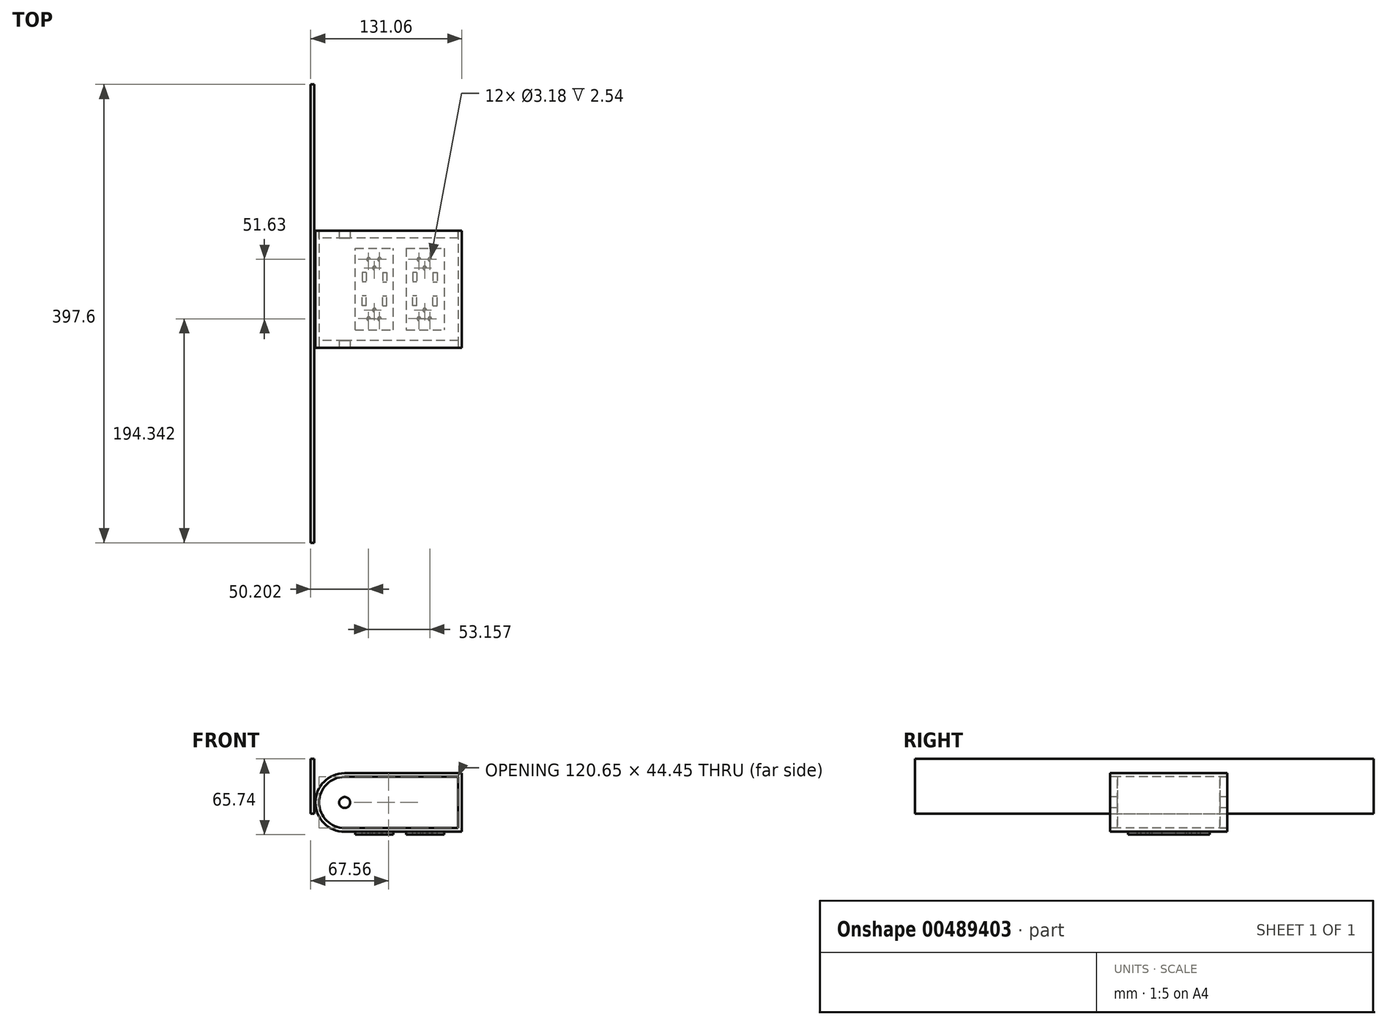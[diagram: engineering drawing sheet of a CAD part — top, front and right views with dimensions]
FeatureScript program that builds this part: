
annotation { "Feature Type Name" : "Feature", "Feature Type Description" : "" }
export const myFeature = defineFeature(function(context is Context, id is Id, definition is map)
    precondition{}
    {
        {
            var Q0;
            Q0=qCreatedBy(makeId("Front.planeOp"),FACE);
            var sketch = newSketch(context, id + "F0", { "sketchPlane" : qUnion([Q0])});
            skLineSegment(sketch, "E0.bottom", {"start": v(0, 0) * mm, "end": v(-101.6, 0) * mm});
            skLineSegment(sketch, "E0.top", {"start": v(0, 50.8) * mm, "end": v(-101.6, 50.8) * mm});
            skLineSegment(sketch, "E0.left", {"start": v(0, 0) * mm, "end": v(0, 50.8) * mm});
            skArc(sketch, "E1", {"start": v(-101.6, 50.8) * mm, "mid": v(-127, 25.4) * mm, "end": v(-101.6, 0) * mm});
            skPoint(sketch, "E1.centerSnap0", {"position": v(-127, 25.4) * mm});
            skArc(sketch, "E2.0", {"start": v(-101.6, 47.62) * mm, "mid": v(-123.83, 25.4) * mm, "end": v(-101.6, 3.18) * mm});
            skLineSegment(sketch, "E2.1", {"start": v(-3.18, 47.62) * mm, "end": v(-101.6, 47.62) * mm});
            skLineSegment(sketch, "E2.2", {"start": v(-3.17, 3.18) * mm, "end": v(-3.18, 47.62) * mm});
            skLineSegment(sketch, "E2.3", {"start": v(-3.17, 3.18) * mm, "end": v(-101.6, 3.17) * mm});
            skCircle(sketch, "E3", {"center": v(-101.6, 25.4) * mm, "radius": 4.76 * mm});
            skSolve(sketch);
        }
        {
            var Q0;
            Q0=makeQuery(id+"F0.imprint","IMPRINT",FACE,{"disambiguationData":[TD([[makeQuery(id+"F0.imprint","IMPRINT",EDGE,{"derivedFrom":sQuery(id+"F0.wireOp",EDGE,"E0.bottom")}),-1.0]])]});
            extrude(context, id + "F1", {"entities" : qUnion([Q0]), "oppositeDirection" : true, "depth" : 101.6 * mm, "offsetDistance" : 25.4 * mm});
        }
        {
            var Q0;
            Q0=makeQuery(id+"F0.imprint","IMPRINT",FACE,{"disambiguationData":[TD([[makeQuery(id+"F0.imprint","IMPRINT",EDGE,{"derivedFrom":sQuery(id+"F0.wireOp",EDGE,"E2.0")}),1.0]])]});
            extrude(context, id + "F2", {"entities" : qUnion([Q0]), "oppositeDirection" : true, "depth" : 6.35 * mm, "offsetDistance" : 25.4 * mm});
        }
        {
            var Q0;
            Q0=makeQuery(id+"F1.opExtrude","CAP_FACE",FACE,{"disambiguationData":[OSD([sQuery(id+"F0.wireOp",EDGE,"E0.bottom"),sQuery(id+"F0.wireOp",EDGE,"E0.top"),sQuery(id+"F0.wireOp",EDGE,"E0.left"),sQuery(id+"F0.wireOp",EDGE,"E1"),sQuery(id+"F0.wireOp",EDGE,"E2.0"),sQuery(id+"F0.wireOp",EDGE,"E2.1"),sQuery(id+"F0.wireOp",EDGE,"E2.2"),sQuery(id+"F0.wireOp",EDGE,"E2.3")])],"isStart":false});
            var sketch = newSketch(context, id + "F3", { "sketchPlane" : qUnion([Q0])});
            skSolve(sketch);
        }
        {
            var Q0;
            Q0=makeQuery(id+"F3.imprint","IMPRINT",FACE,{"disambiguationData":[TD([[makeQuery(id+"F3.imprint","IMPRINT",EDGE,{"derivedFrom":makeQuery(id+"F1.opExtrude","CAP_EDGE",EDGE,{"disambiguationData":[OSD([sQuery(id+"F0.wireOp",EDGE,"E2.0")])],"isStart":false})}),-1.0]])]});
            extrude(context, id + "F4", {"entities" : qUnion([Q0]), "oppositeDirection" : true, "depth" : 6.35 * mm, "offsetDistance" : 25.4 * mm});
        }
        {
            var Q0;
            Q0=makeQuery(id+"F1.opExtrude","SWEPT_FACE",FACE,{"disambiguationData":[OSD([sQuery(id+"F0.wireOp",EDGE,"E0.bottom")])]});
            var sketch = newSketch(context, id + "F5", { "sketchPlane" : qUnion([Q0])});
            skLineSegment(sketch, "E4.bottom", {"start": v(-92.53, -15.52) * mm, "end": v(-59.53, -15.52) * mm});
            skLineSegment(sketch, "E4.top", {"start": v(-92.53, -86.52) * mm, "end": v(-59.53, -86.52) * mm});
            skLineSegment(sketch, "E4.left", {"start": v(-92.53, -15.52) * mm, "end": v(-92.53, -86.52) * mm});
            skLineSegment(sketch, "E4.right", {"start": v(-59.53, -15.52) * mm, "end": v(-59.53, -86.52) * mm});
            skLineSegment(sketch, "E5.bottom", {"start": v(-48.24, -86.52) * mm, "end": v(-15.25, -86.52) * mm});
            skLineSegment(sketch, "E5.top", {"start": v(-48.24, -15.52) * mm, "end": v(-15.25, -15.52) * mm});
            skLineSegment(sketch, "E5.left", {"start": v(-48.24, -86.52) * mm, "end": v(-48.24, -15.52) * mm});
            skLineSegment(sketch, "E5.right", {"start": v(-15.25, -86.52) * mm, "end": v(-15.25, -15.52) * mm});
            skCircle(sketch, "E6", {"center": v(-80.86, -25.3) * mm, "radius": 1.59 * mm});
            skCircle(sketch, "E7", {"center": v(-71.39, -25.2) * mm, "radius": 1.59 * mm});
            skCircle(sketch, "E8", {"center": v(-75.83, -32.77) * mm, "radius": 1.59 * mm});
            skLineSegment(sketch, "E9.bottom", {"start": v(-68.76, -36.47) * mm, "end": v(-65.13, -36.47) * mm});
            skLineSegment(sketch, "E9.top", {"start": v(-68.76, -44.95) * mm, "end": v(-65.13, -44.95) * mm});
            skLineSegment(sketch, "E9.left", {"start": v(-68.76, -36.47) * mm, "end": v(-68.76, -44.95) * mm});
            skLineSegment(sketch, "E9.right", {"start": v(-65.13, -36.47) * mm, "end": v(-65.13, -44.95) * mm});
            skLineSegment(sketch, "E10.bottom", {"start": v(-82.86, -36.47) * mm, "end": v(-86.27, -36.47) * mm});
            skLineSegment(sketch, "E10.top", {"start": v(-82.86, -44.95) * mm, "end": v(-86.27, -44.95) * mm});
            skLineSegment(sketch, "E10.left", {"start": v(-82.86, -36.47) * mm, "end": v(-82.86, -44.95) * mm});
            skLineSegment(sketch, "E10.right", {"start": v(-86.27, -36.47) * mm, "end": v(-86.27, -44.95) * mm});
            skLineSegment(sketch, "E11.1.0.0", {"start": v(-25.08, -36.47) * mm, "end": v(-25.08, -44.95) * mm});
            skLineSegment(sketch, "E11.1.0.1", {"start": v(-21.44, -36.47) * mm, "end": v(-21.44, -44.95) * mm});
            skCircle(sketch, "E11.1.0.2", {"center": v(-32.14, -32.77) * mm, "radius": 1.59 * mm});
            skLineSegment(sketch, "E11.1.0.3", {"start": v(-42.58, -36.47) * mm, "end": v(-42.58, -44.95) * mm});
            skCircle(sketch, "E11.1.0.4", {"center": v(-37.17, -25.3) * mm, "radius": 1.59 * mm});
            skCircle(sketch, "E11.1.0.5", {"center": v(-27.7, -25.2) * mm, "radius": 1.59 * mm});
            skLineSegment(sketch, "E11.1.0.6", {"start": v(-39.17, -36.47) * mm, "end": v(-39.17, -44.95) * mm});
            skLineSegment(sketch, "E11.1.0.7", {"start": v(-39.17, -36.47) * mm, "end": v(-42.58, -36.47) * mm});
            skLineSegment(sketch, "E11.1.0.8", {"start": v(-25.08, -36.47) * mm, "end": v(-21.44, -36.47) * mm});
            skLineSegment(sketch, "E11.1.0.9", {"start": v(-25.08, -44.95) * mm, "end": v(-21.44, -44.95) * mm});
            skLineSegment(sketch, "E11.1.0.10", {"start": v(-39.17, -44.95) * mm, "end": v(-42.58, -44.95) * mm});
            skLineSegment(sketch, "E11.direction1", {"start": v(-86.27, -44.95) * mm, "end": v(-42.58, -44.95) * mm, "construction": true});
            skLineSegment(sketch, "E12", {"start": v(-92.53, -51.02) * mm, "end": v(-15.25, -51.02) * mm, "construction": true});
            skLineSegment(sketch, "E13.MirrorCS", {"start": v(-82.86, -57.09) * mm, "end": v(-86.27, -57.09) * mm});
            skLineSegment(sketch, "E14.MirrorCS", {"start": v(-82.86, -65.57) * mm, "end": v(-86.27, -65.57) * mm});
            skLineSegment(sketch, "E15.MirrorCS", {"start": v(-68.76, -57.09) * mm, "end": v(-65.13, -57.09) * mm});
            skLineSegment(sketch, "E16.MirrorCS", {"start": v(-68.76, -65.57) * mm, "end": v(-65.13, -65.57) * mm});
            skLineSegment(sketch, "E17.MirrorCS", {"start": v(-86.27, -65.57) * mm, "end": v(-86.27, -57.09) * mm});
            skLineSegment(sketch, "E18.MirrorCS", {"start": v(-68.76, -65.57) * mm, "end": v(-68.76, -57.09) * mm});
            skLineSegment(sketch, "E19.MirrorCS", {"start": v(-82.86, -65.57) * mm, "end": v(-82.86, -57.09) * mm});
            skCircle(sketch, "E20.MirrorC", {"center": v(-75.83, -69.27) * mm, "radius": 1.59 * mm});
            skLineSegment(sketch, "E21.MirrorCS", {"start": v(-65.13, -65.57) * mm, "end": v(-65.13, -57.09) * mm});
            skCircle(sketch, "E22.MirrorC", {"center": v(-71.39, -76.83) * mm, "radius": 1.59 * mm});
            skCircle(sketch, "E23.MirrorC", {"center": v(-80.86, -76.74) * mm, "radius": 1.59 * mm});
            skLineSegment(sketch, "E24.MirrorCS", {"start": v(-25.08, -57.09) * mm, "end": v(-21.44, -57.09) * mm});
            skLineSegment(sketch, "E25.MirrorCS", {"start": v(-25.08, -65.57) * mm, "end": v(-21.44, -65.57) * mm});
            skLineSegment(sketch, "E26.MirrorCS", {"start": v(-39.17, -65.57) * mm, "end": v(-42.58, -65.57) * mm});
            skLineSegment(sketch, "E27.MirrorCS", {"start": v(-39.17, -57.09) * mm, "end": v(-42.58, -57.09) * mm});
            skCircle(sketch, "E28.MirrorC", {"center": v(-32.14, -69.27) * mm, "radius": 1.59 * mm});
            skCircle(sketch, "E29.MirrorC", {"center": v(-27.7, -76.83) * mm, "radius": 1.59 * mm});
            skLineSegment(sketch, "E30.MirrorCS", {"start": v(-39.17, -65.57) * mm, "end": v(-39.17, -57.09) * mm});
            skCircle(sketch, "E31.MirrorC", {"center": v(-37.17, -76.74) * mm, "radius": 1.59 * mm});
            skLineSegment(sketch, "E32.MirrorCS", {"start": v(-42.58, -65.57) * mm, "end": v(-42.58, -57.09) * mm});
            skLineSegment(sketch, "E33.MirrorCS", {"start": v(-25.08, -65.57) * mm, "end": v(-25.08, -57.09) * mm});
            skLineSegment(sketch, "E34.MirrorCS", {"start": v(-21.44, -65.57) * mm, "end": v(-21.44, -57.09) * mm});
            skSolve(sketch);
        }
        {
            var Q0;
            Q0=makeQuery(id+"F5.imprint","IMPRINT",FACE,{"disambiguationData":[TD([[makeQuery(id+"F5.imprint","IMPRINT",EDGE,{"derivedFrom":sQuery(id+"F5.wireOp",EDGE,"E4.bottom")}),-1.0]])]});
            var Q1;
            Q1=makeQuery(id+"F5.imprint","IMPRINT",FACE,{"disambiguationData":[TD([[makeQuery(id+"F5.imprint","IMPRINT",EDGE,{"derivedFrom":sQuery(id+"F5.wireOp",EDGE,"E5.bottom")}),1.0]])]});
            extrude(context, id + "F6", {"entities" : qUnion([Q0, Q1]), "operationType" : NewBodyOperationType.ADD, "depth" : 2.54 * mm, "offsetDistance" : 25.4 * mm});
        }
        {
            var Q0;
            Q0=makeQuery(id+"F0.imprint","IMPRINT",FACE,{"disambiguationData":[TD([[makeQuery(id+"F0.imprint","IMPRINT",EDGE,{"derivedFrom":sQuery(id+"F0.wireOp",EDGE,"E3")}),1.0]])]});
            var Q1;
            Q1=makeQuery(id+"F1.opExtrude","CAP_FACE",FACE,{"disambiguationData":[OSD([sQuery(id+"F0.wireOp",EDGE,"E0.bottom"),sQuery(id+"F0.wireOp",EDGE,"E0.top"),sQuery(id+"F0.wireOp",EDGE,"E0.left"),sQuery(id+"F0.wireOp",EDGE,"E1"),sQuery(id+"F0.wireOp",EDGE,"E2.0"),sQuery(id+"F0.wireOp",EDGE,"E2.1"),sQuery(id+"F0.wireOp",EDGE,"E2.2"),sQuery(id+"F0.wireOp",EDGE,"E2.3")])],"isStart":false});
            extrude(context, id + "F7", {"entities" : qUnion([Q0]), "operationType" : NewBodyOperationType.REMOVE, "oppositeDirection" : true, "depth" : 152.4 * mm, "endBoundEntityFace" : qUnion([Q1]), "offsetDistance" : 25.4 * mm});
        }
        {
            var Q0;
            Q0=qCreatedBy(makeId("Right.planeOp"),FACE);
            cPlane(context, id + "F8", {"entities" : qUnion([Q0]), "cplaneType" : CPlaneType.OFFSET, "offset" : 131.06 * mm, "oppositeDirection" : true, "width" : 152.4 * mm, "height" : 152.4 * mm});
        }
        {
            var Q0;
            Q0=qCreatedBy(id+"F8.planeOp",FACE);
            var sketch = newSketch(context, id + "F9", { "sketchPlane" : qUnion([Q0])});
            skLineSegment(sketch, "E35", {"start": v(228.46, 63.2) * mm, "end": v(-169.14, 63.2) * mm});
            skLineSegment(sketch, "E36", {"start": v(-169.14, 63.2) * mm, "end": v(-169.14, 15.57) * mm});
            skLineSegment(sketch, "E37", {"start": v(-169.14, 15.57) * mm, "end": v(228.46, 15.57) * mm});
            skLineSegment(sketch, "E38", {"start": v(228.46, 15.57) * mm, "end": v(228.46, 63.2) * mm});
            skSolve(sketch);
        }
        {
            var Q0;
            Q0=makeQuery(id+"F9.imprint","IMPRINT",FACE,{"disambiguationData":[TD([[makeQuery(id+"F9.imprint","IMPRINT",EDGE,{"derivedFrom":sQuery(id+"F9.wireOp",EDGE,"E35")}),1.0]])]});
            extrude(context, id + "F10", {"entities" : qUnion([Q0]), "depth" : 3.17 * mm, "offsetDistance" : 25.4 * mm});
        }
    });
